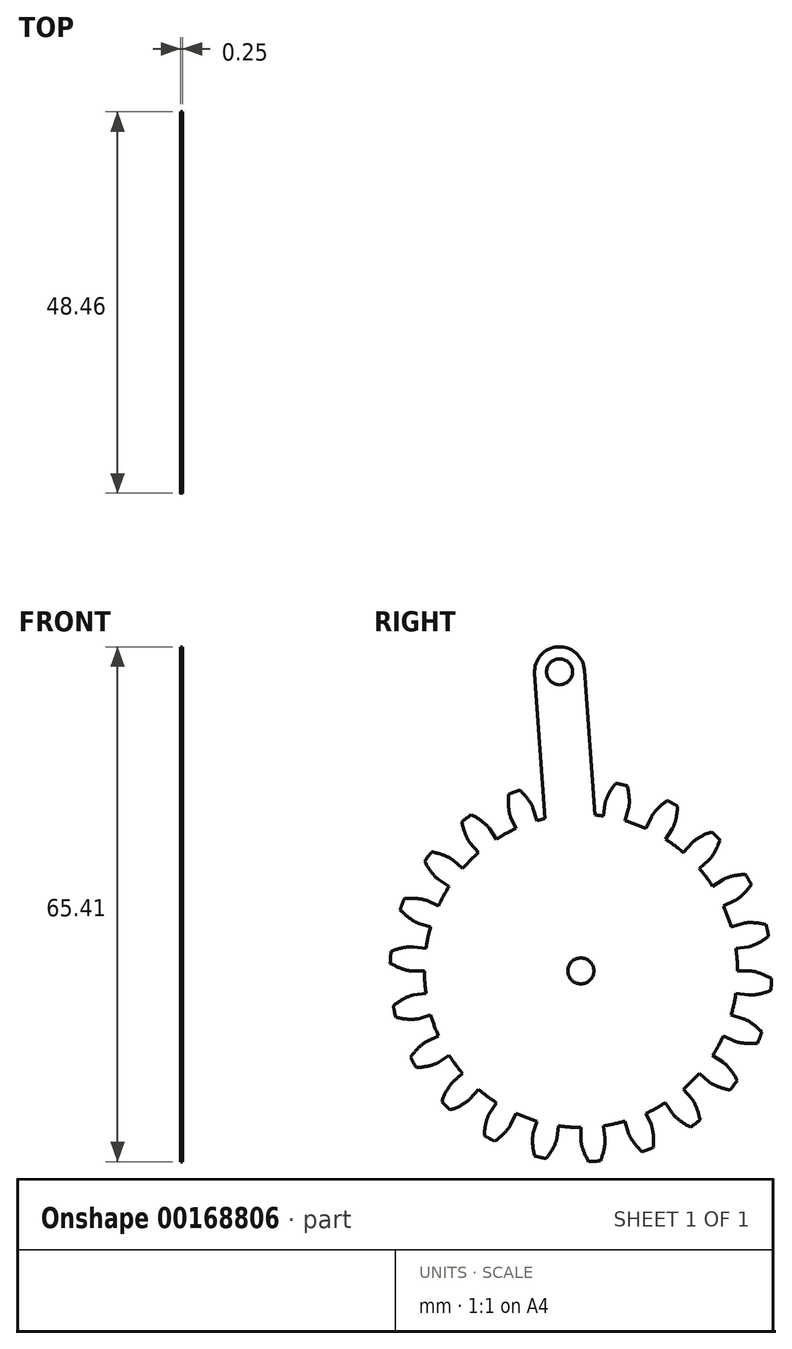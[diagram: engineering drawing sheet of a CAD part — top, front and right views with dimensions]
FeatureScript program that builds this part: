
annotation { "Feature Type Name" : "Feature", "Feature Type Description" : "" }
export const myFeature = defineFeature(function(context is Context, id is Id, definition is map)
    precondition{}
    {
        {
            assignVariable(context, id + "F0", {"name" : "NumberTeeth", "anyValue" : 22});
        }
        {
            assignVariable(context, id + "F1", {"name" : "GearThickness", "anyValue" : 0.25});
        }
        {
            var Q0;
            Q0=qCreatedBy(makeId("Right.planeOp"),FACE);
            var sketch = newSketch(context, id + "F2", { "sketchPlane" : qUnion([Q0])});
            skCircle(sketch, "E0", {"center": v(0, 0) * mm, "radius": 19.89 * mm});
            skCircle(sketch, "E1", {"center": v(0, 0) * mm, "radius": 21.52 * mm, "construction": true});
            skCircle(sketch, "E2", {"center": v(0, 0) * mm, "radius": 22.22 * mm, "construction": true});
            skCircle(sketch, "E3", {"center": v(0, 0) * mm, "radius": 24.25 * mm});
            skLineSegment(sketch, "E4", {"start": v(0, 0) * mm, "end": v(-21.52, 0) * mm, "construction": true});
            skLineSegment(sketch, "E5.1.0", {"start": v(0, 0) * mm, "end": v(-21.5, 1.08) * mm, "construction": true});
            skLineSegment(sketch, "E5.2.0", {"start": v(0, 0) * mm, "end": v(-21.4, 2.15) * mm, "construction": true});
            skLineSegment(sketch, "E5.3.0", {"start": v(0, 0) * mm, "end": v(-21.28, 3.22) * mm, "construction": true});
            skLineSegment(sketch, "E5.4.0", {"start": v(0, 0) * mm, "end": v(-21.09, 4.27) * mm, "construction": true});
            skLineSegment(sketch, "E5.5.0", {"start": v(0, 0) * mm, "end": v(-20.85, 5.32) * mm, "construction": true});
            skLineSegment(sketch, "E5.6.0", {"start": v(0, 0) * mm, "end": v(-20.56, 6.36) * mm, "construction": true});
            skLineSegment(sketch, "E5.7.0", {"start": v(0, 0) * mm, "end": v(-20.21, 7.38) * mm, "construction": true});
            skLineSegment(sketch, "E5.8.0", {"start": v(0, 0) * mm, "end": v(-19.82, 8.38) * mm, "construction": true});
            skLineSegment(sketch, "E5.9.0", {"start": v(0, 0) * mm, "end": v(-19.37, 9.36) * mm, "construction": true});
            skLineSegment(sketch, "E5.10.0", {"start": v(0, 0) * mm, "end": v(-18.88, 10.32) * mm, "construction": true});
            skLineSegment(sketch, "E5.11.0", {"start": v(0, 0) * mm, "end": v(-18.34, 11.25) * mm, "construction": true});
            skLineSegment(sketch, "E5.12.0", {"start": v(0, 0) * mm, "end": v(-17.76, 12.15) * mm, "construction": true});
            skLineSegment(sketch, "E5.13.0", {"start": v(0, 0) * mm, "end": v(-17.13, 13.02) * mm, "construction": true});
            skLineSegment(sketch, "E5.14.0", {"start": v(0, 0) * mm, "end": v(-16.46, 13.86) * mm, "construction": true});
            skLineSegment(sketch, "E5.anchor2", {"start": v(0, 0) * mm, "end": v(-16.46, 13.86) * mm, "construction": true});
            skLineSegment(sketch, "E6", {"start": v(-21.5, 1.08) * mm, "end": v(-21.54, 0) * mm, "construction": true});
            skLineSegment(sketch, "E7", {"start": v(-21.4, 2.15) * mm, "end": v(-21.62, 0) * mm, "construction": true});
            skLineSegment(sketch, "E8", {"start": v(-21.28, 3.22) * mm, "end": v(-21.76, 0.02) * mm, "construction": true});
            skLineSegment(sketch, "E9", {"start": v(-20.85, 5.32) * mm, "end": v(-22.18, 0.11) * mm, "construction": true});
            skLineSegment(sketch, "E10", {"start": v(-20.56, 6.36) * mm, "end": v(-22.46, 0.2) * mm, "construction": true});
            skLineSegment(sketch, "E11", {"start": v(-20.21, 7.38) * mm, "end": v(-22.8, 0.3) * mm, "construction": true});
            skLineSegment(sketch, "E12", {"start": v(-19.82, 8.38) * mm, "end": v(-23.17, 0.45) * mm, "construction": true});
            skLineSegment(sketch, "E13", {"start": v(-19.37, 9.36) * mm, "end": v(-23.59, 0.64) * mm, "construction": true});
            skLineSegment(sketch, "E14", {"start": v(-18.88, 10.32) * mm, "end": v(-24.04, 0.87) * mm, "construction": true});
            skLineSegment(sketch, "E15", {"start": v(-18.34, 11.25) * mm, "end": v(-24.53, 1.16) * mm, "construction": true});
            skLineSegment(sketch, "E16", {"start": v(-21.09, 4.27) * mm, "end": v(-21.94, 0.06) * mm, "construction": true});
            skLineSegment(sketch, "E17", {"start": v(-17.76, 12.15) * mm, "end": v(-25.05, 1.5) * mm, "construction": true});
            skLineSegment(sketch, "E18", {"start": v(-17.13, 13.02) * mm, "end": v(-25.6, 1.89) * mm, "construction": true});
            skLineSegment(sketch, "E19", {"start": v(-16.46, 13.86) * mm, "end": v(-26.16, 2.34) * mm, "construction": true});
            skLineSegment(sketch, "E20", {"start": v(0, 0) * mm, "end": v(-21.46, 1.54) * mm, "construction": true});
            skLineSegment(sketch, "E21", {"start": v(-19.89, 0) * mm, "end": v(-21.52, 0) * mm});
            skLineSegment(sketch, "E22.MirrorCS", {"start": v(-19.68, 2.83) * mm, "end": v(-21.3, 3.06) * mm});
            skFitSpline(sketch, "E23", {"points": [v(-21.52, 0) * mm, v(-21.54, 0) * mm, v(-21.62, 0) * mm, v(-21.76, 0.02) * mm, v(-21.94, 0.06) * mm, v(-22.18, 0.11) * mm, v(-22.46, 0.2) * mm, v(-22.8, 0.3) * mm, v(-23.17, 0.45) * mm, v(-23.59, 0.64) * mm, v(-24.04, 0.87) * mm, v(-24.53, 1.16) * mm, v(-25.05, 1.5) * mm, v(-25.6, 1.89) * mm, v(-26.16, 2.34) * mm], "startDerivative": vector(-0.77, 0) * mm, "endDerivative": vector(-1.36, 1.15) * mm});
            skLineSegment(sketch, "E24", {"start": v(-21.81, -1.32) * mm, "end": v(-26.16, 2.34) * mm, "construction": true});
            skFitSpline(sketch, "E25.MirrorCS", {"points": [v(-21.3, 3.06) * mm, v(-21.32, 3.07) * mm, v(-21.4, 3.07) * mm, v(-21.54, 3.07) * mm, v(-21.73, 3.07) * mm, v(-21.97, 3.05) * mm, v(-22.26, 3) * mm, v(-22.6, 2.94) * mm, v(-23, 2.85) * mm, v(-23.44, 2.72) * mm, v(-23.92, 2.56) * mm, v(-24.44, 2.35) * mm, v(-25, 2.09) * mm, v(-25.6, 1.77) * mm, v(-26.23, 1.4) * mm], "startDerivative": vector(-0.77, 0.11) * mm, "endDerivative": vector(-1.51, -0.94) * mm});
            skSolve(sketch);
        }
        {
            var Q0;
            {var subQ0=sQuery(id+"F2.wireOp",EDGE,"E0");var subQ27=makeQuery(id+"F2.imprint","INTERSECT",VERTEX,{"derivedFrom":[subQ0,sQuery(id+"F2.wireOp",EDGE,"10ea1024-8cf5-41f5-a75f-a634b86921f3.10.0")]});Q0=makeQuery(id+"F2.imprint","IMPRINT",FACE,{"disambiguationData":[TD([[makeQuery(id+"F2.imprint","IMPRINT",EDGE,{"disambiguationData":[TD([[subQ27,-1.0]])],"derivedFrom":subQ0}),1.0]])]});}
            var Q1;
            {var subQ0=sQuery(id+"F2.wireOp",EDGE,"10ea1024-8cf5-41f5-a75f-a634b86921f3.1.0");Q1=makeQuery(id+"F2.imprint","IMPRINT",FACE,{"disambiguationData":[TD([[makeQuery(id+"F2.imprint","IMPRINT",EDGE,{"derivedFrom":subQ0}),-1.0]])]});}
            var Q2;
            {var subQ7=sQuery(id+"F2.wireOp",EDGE,"10ea1024-8cf5-41f5-a75f-a634b86921f3.2.0");Q2=makeQuery(id+"F2.imprint","IMPRINT",FACE,{"disambiguationData":[TD([[makeQuery(id+"F2.imprint","IMPRINT",EDGE,{"derivedFrom":subQ7}),-1.0]])]});}
            var Q3;
            {var subQ8=sQuery(id+"F2.wireOp",EDGE,"10ea1024-8cf5-41f5-a75f-a634b86921f3.3.0");Q3=makeQuery(id+"F2.imprint","IMPRINT",FACE,{"disambiguationData":[TD([[makeQuery(id+"F2.imprint","IMPRINT",EDGE,{"derivedFrom":subQ8}),-1.0]])]});}
            var Q4;
            {var subQ2=sQuery(id+"F2.wireOp",EDGE,"10ea1024-8cf5-41f5-a75f-a634b86921f3.4.0");Q4=makeQuery(id+"F2.imprint","IMPRINT",FACE,{"disambiguationData":[TD([[makeQuery(id+"F2.imprint","IMPRINT",EDGE,{"derivedFrom":subQ2}),-1.0]])]});}
            var Q5;
            {var subQ8=sQuery(id+"F2.wireOp",EDGE,"10ea1024-8cf5-41f5-a75f-a634b86921f3.5.0");Q5=makeQuery(id+"F2.imprint","IMPRINT",FACE,{"disambiguationData":[TD([[makeQuery(id+"F2.imprint","IMPRINT",EDGE,{"derivedFrom":subQ8}),-1.0]])]});}
            var Q6;
            {var subQ3=sQuery(id+"F2.wireOp",EDGE,"10ea1024-8cf5-41f5-a75f-a634b86921f3.6.0");Q6=makeQuery(id+"F2.imprint","IMPRINT",FACE,{"disambiguationData":[TD([[makeQuery(id+"F2.imprint","IMPRINT",EDGE,{"derivedFrom":subQ3}),-1.0]])]});}
            var Q7;
            {var subQ0=sQuery(id+"F2.wireOp",EDGE,"10ea1024-8cf5-41f5-a75f-a634b86921f3.7.0");Q7=makeQuery(id+"F2.imprint","IMPRINT",FACE,{"disambiguationData":[TD([[makeQuery(id+"F2.imprint","IMPRINT",EDGE,{"derivedFrom":subQ0}),-1.0]])]});}
            var Q8;
            {var subQ5=sQuery(id+"F2.wireOp",EDGE,"10ea1024-8cf5-41f5-a75f-a634b86921f3.8.0");Q8=makeQuery(id+"F2.imprint","IMPRINT",FACE,{"disambiguationData":[TD([[makeQuery(id+"F2.imprint","IMPRINT",EDGE,{"derivedFrom":subQ5}),-1.0]])]});}
            var Q9;
            {var subQ1=sQuery(id+"F2.wireOp",EDGE,"10ea1024-8cf5-41f5-a75f-a634b86921f3.9.0");Q9=makeQuery(id+"F2.imprint","IMPRINT",FACE,{"disambiguationData":[TD([[makeQuery(id+"F2.imprint","IMPRINT",EDGE,{"derivedFrom":subQ1}),-1.0]])]});}
            var Q10;
            {var subQ5=sQuery(id+"F2.wireOp",EDGE,"10ea1024-8cf5-41f5-a75f-a634b86921f3.10.0");Q10=makeQuery(id+"F2.imprint","IMPRINT",FACE,{"disambiguationData":[TD([[makeQuery(id+"F2.imprint","IMPRINT",EDGE,{"derivedFrom":subQ5}),-1.0]])]});}
            var Q11;
            {var subQ8=sQuery(id+"F2.wireOp",EDGE,"10ea1024-8cf5-41f5-a75f-a634b86921f3.11.0");Q11=makeQuery(id+"F2.imprint","IMPRINT",FACE,{"disambiguationData":[TD([[makeQuery(id+"F2.imprint","IMPRINT",EDGE,{"derivedFrom":subQ8}),-1.0]])]});}
            var Q12;
            {var subQ2=sQuery(id+"F2.wireOp",EDGE,"10ea1024-8cf5-41f5-a75f-a634b86921f3.12.0");Q12=makeQuery(id+"F2.imprint","IMPRINT",FACE,{"disambiguationData":[TD([[makeQuery(id+"F2.imprint","IMPRINT",EDGE,{"derivedFrom":subQ2}),-1.0]])]});}
            var Q13;
            {var subQ3=sQuery(id+"F2.wireOp",EDGE,"10ea1024-8cf5-41f5-a75f-a634b86921f3.13.0");Q13=makeQuery(id+"F2.imprint","IMPRINT",FACE,{"disambiguationData":[TD([[makeQuery(id+"F2.imprint","IMPRINT",EDGE,{"derivedFrom":subQ3}),-1.0]])]});}
            var Q14;
            {var subQ0=sQuery(id+"F2.wireOp",EDGE,"10ea1024-8cf5-41f5-a75f-a634b86921f3.14.0");Q14=makeQuery(id+"F2.imprint","IMPRINT",FACE,{"disambiguationData":[TD([[makeQuery(id+"F2.imprint","IMPRINT",EDGE,{"derivedFrom":subQ0}),-1.0]])]});}
            var Q15;
            {var subQ6=sQuery(id+"F2.wireOp",EDGE,"10ea1024-8cf5-41f5-a75f-a634b86921f3.15.0");Q15=makeQuery(id+"F2.imprint","IMPRINT",FACE,{"disambiguationData":[TD([[makeQuery(id+"F2.imprint","IMPRINT",EDGE,{"derivedFrom":subQ6}),-1.0]])]});}
            var Q16;
            {var subQ5=sQuery(id+"F2.wireOp",EDGE,"10ea1024-8cf5-41f5-a75f-a634b86921f3.16.0");Q16=makeQuery(id+"F2.imprint","IMPRINT",FACE,{"disambiguationData":[TD([[makeQuery(id+"F2.imprint","IMPRINT",EDGE,{"derivedFrom":subQ5}),-1.0]])]});}
            var Q17;
            {var subQ7=sQuery(id+"F2.wireOp",EDGE,"10ea1024-8cf5-41f5-a75f-a634b86921f3.17.0");Q17=makeQuery(id+"F2.imprint","IMPRINT",FACE,{"disambiguationData":[TD([[makeQuery(id+"F2.imprint","IMPRINT",EDGE,{"derivedFrom":subQ7}),-1.0]])]});}
            var Q18;
            {var subQ5=sQuery(id+"F2.wireOp",EDGE,"10ea1024-8cf5-41f5-a75f-a634b86921f3.18.0");Q18=makeQuery(id+"F2.imprint","IMPRINT",FACE,{"disambiguationData":[TD([[makeQuery(id+"F2.imprint","IMPRINT",EDGE,{"derivedFrom":subQ5}),-1.0]])]});}
            var Q19;
            {var subQ8=sQuery(id+"F2.wireOp",EDGE,"10ea1024-8cf5-41f5-a75f-a634b86921f3.19.0");Q19=makeQuery(id+"F2.imprint","IMPRINT",FACE,{"disambiguationData":[TD([[makeQuery(id+"F2.imprint","IMPRINT",EDGE,{"derivedFrom":subQ8}),-1.0]])]});}
            var Q20;
            {var subQ8=sQuery(id+"F2.wireOp",EDGE,"E21");Q20=makeQuery(id+"F2.imprint","IMPRINT",FACE,{"disambiguationData":[TD([[makeQuery(id+"F2.imprint","IMPRINT",EDGE,{"derivedFrom":subQ8}),-1.0]])]});}
            extrude(context, id + "F3", {"entities" : qUnion([Q0, Q1, Q2, Q3, Q4, Q5, Q6, Q7, Q8, Q9, Q10, Q11, Q12, Q13, Q14, Q15, Q16, Q17, Q18, Q19, Q20]), "depth" : (getVariable(context, 'GearThickness')) * mm});
        }
        {
            var Q0;
            Q0=makeQuery(id+"F3.opExtrude","SWEPT_FACE",FACE,{"disambiguationData":[OSD([sQuery(id+"F2.wireOp",EDGE,"E25.MirrorCS")])]});
            var Q1;
            Q1=makeQuery(id+"F3.opExtrude","SWEPT_FACE",FACE,{"disambiguationData":[OSD([sQuery(id+"F2.wireOp",EDGE,"E23")])]});
            var Q2;
            Q2=makeQuery(id+"F3.opExtrude","SWEPT_FACE",FACE,{"disambiguationData":[OSD([sQuery(id+"F2.wireOp",EDGE,"E3")])]});
            var Q3;
            Q3=makeQuery(id+"F3.opExtrude","SWEPT_FACE",FACE,{"disambiguationData":[OSD([sQuery(id+"F2.wireOp",EDGE,"E22.MirrorCS")])]});
            var Q4;
            Q4=makeQuery(id+"F3.opExtrude","SWEPT_FACE",FACE,{"disambiguationData":[OSD([sQuery(id+"F2.wireOp",EDGE,"E21")])]});
            var Q5;
            Q5=makeQuery(id+"F3.opExtrude","SWEPT_FACE",FACE,{"disambiguationData":[OSD([sQuery(id+"F2.wireOp",EDGE,"E0")])]});
            circularPattern(context, id + "F4", {"faces" : qUnion([Q0, Q1, Q2, Q3, Q4]), "axis" : qUnion([Q5]), "angle" : 360 * degree, "instanceCount" : getVariable(context, 'NumberTeeth'), "equalSpace" : true, "patternType" : PatternType.FACE});
        }
        {
            var Q0;
            Q0=makeQuery(id+"F3.opExtrude","CAP_FACE",FACE,{"disambiguationData":[OSD([sQuery(id+"F2.wireOp",EDGE,"E0"),sQuery(id+"F2.wireOp",EDGE,"E3"),sQuery(id+"F2.wireOp",EDGE,"E21"),sQuery(id+"F2.wireOp",EDGE,"E22.MirrorCS"),sQuery(id+"F2.wireOp",EDGE,"E23"),sQuery(id+"F2.wireOp",EDGE,"E25.MirrorCS")])],"isStart":false});
            var sketch = newSketch(context, id + "F5", { "sketchPlane" : qUnion([Q0])});
            skCircle(sketch, "E26", {"center": v(0, 0) * mm, "radius": 1.65 * mm});
            skSolve(sketch);
        }
        {
            var Q0;
            Q0 = qSketchRegion(id + "F5", true);
            var Q1;
            Q1=makeQuery(id+"F3.opExtrude","CAP_FACE",FACE,{"disambiguationData":[OSD([sQuery(id+"F2.wireOp",EDGE,"E0"),sQuery(id+"F2.wireOp",EDGE,"E3"),sQuery(id+"F2.wireOp",EDGE,"E21"),sQuery(id+"F2.wireOp",EDGE,"E22.MirrorCS"),sQuery(id+"F2.wireOp",EDGE,"E23"),sQuery(id+"F2.wireOp",EDGE,"E25.MirrorCS")])],"isStart":true});
            extrude(context, id + "F6", {"entities" : qUnion([Q0]), "operationType" : NewBodyOperationType.REMOVE, "endBound" : BoundingType.UP_TO_SURFACE, "oppositeDirection" : true, "endBoundEntityFace" : qUnion([Q1]), "depth" : 25.4 * mm});
        }
        {
            var Q0;
            Q0=makeQuery(id+"F3.opExtrude","CAP_FACE",FACE,{"disambiguationData":[OSD([sQuery(id+"F2.wireOp",EDGE,"E0"),sQuery(id+"F2.wireOp",EDGE,"E3"),sQuery(id+"F2.wireOp",EDGE,"E21"),sQuery(id+"F2.wireOp",EDGE,"E22.MirrorCS"),sQuery(id+"F2.wireOp",EDGE,"E23"),sQuery(id+"F2.wireOp",EDGE,"E25.MirrorCS")])],"isStart":false});
            var sketch = newSketch(context, id + "F7", { "sketchPlane" : qUnion([Q0])});
            skLineSegment(sketch, "E27", {"start": v(0, 0) * mm, "end": v(-1.73, 24.18) * mm});
            skLineSegment(sketch, "E28", {"start": v(-1.73, 24.18) * mm, "end": v(-2.72, 38) * mm});
            skCircle(sketch, "E29", {"center": v(-2.72, 38) * mm, "radius": 1.65 * mm});
            skLineSegment(sketch, "E30", {"start": v(-6.11, 40.94) * mm, "end": v(-2.94, -3.4) * mm});
            skLineSegment(sketch, "E31", {"start": v(0.22, 41.4) * mm, "end": v(3.4, -2.94) * mm});
            skLineSegment(sketch, "E32", {"start": v(-6.11, 40.94) * mm, "end": v(0.22, 41.4) * mm});
            skLineSegment(sketch, "E33", {"start": v(-2.94, -3.4) * mm, "end": v(3.4, -2.94) * mm});
            skSolve(sketch);
        }
        {
            var Q0;
            Q0 = qSketchRegion(id + "F7", true);
            var Q1;
            Q1=makeQuery(id+"F3.opExtrude","CAP_FACE",FACE,{"disambiguationData":[OSD([sQuery(id+"F2.wireOp",EDGE,"E0"),sQuery(id+"F2.wireOp",EDGE,"E3"),sQuery(id+"F2.wireOp",EDGE,"E21"),sQuery(id+"F2.wireOp",EDGE,"E22.MirrorCS"),sQuery(id+"F2.wireOp",EDGE,"E23"),sQuery(id+"F2.wireOp",EDGE,"E25.MirrorCS")])],"isStart":true});
            extrude(context, id + "F8", {"entities" : qUnion([Q0]), "operationType" : NewBodyOperationType.ADD, "endBound" : BoundingType.UP_TO_SURFACE, "oppositeDirection" : true, "endBoundEntityFace" : qUnion([Q1]), "depth" : 25.4 * mm});
        }
        {
            var Q0;
            Q0=makeQuery(id+"F8.boolean.opBoolean","MERGE",FACE,{"derivedFrom":[makeQuery(id+"F3.opExtrude","CAP_FACE",FACE,{"disambiguationData":[OSD([sQuery(id+"F2.wireOp",EDGE,"E0"),sQuery(id+"F2.wireOp",EDGE,"E3"),sQuery(id+"F2.wireOp",EDGE,"E21"),sQuery(id+"F2.wireOp",EDGE,"E22.MirrorCS"),sQuery(id+"F2.wireOp",EDGE,"E23"),sQuery(id+"F2.wireOp",EDGE,"E25.MirrorCS")])],"isStart":false}),makeQuery(id+"F8.opExtrude","CAP_FACE",FACE,{"disambiguationData":[OSD([sQuery(id+"F7.wireOp",EDGE,"E29"),sQuery(id+"F7.wireOp",EDGE,"E30"),sQuery(id+"F7.wireOp",EDGE,"E31"),sQuery(id+"F7.wireOp",EDGE,"E32"),sQuery(id+"F7.wireOp",EDGE,"E33")])],"isStart":true})]});
            var sketch = newSketch(context, id + "F9", { "sketchPlane" : qUnion([Q0])});
            skCircle(sketch, "E34", {"center": v(0, 0) * mm, "radius": 1.65 * mm});
            skSolve(sketch);
        }
        {
            var Q0;
            Q0 = qSketchRegion(id + "F9", true);
            var Q1;
            {var subQ0=sQuery(id+"F2.wireOp",EDGE,"E25.MirrorCS");var subQ1=sQuery(id+"F2.wireOp",EDGE,"E23");var subQ2=sQuery(id+"F2.wireOp",EDGE,"E22.MirrorCS");var subQ3=sQuery(id+"F2.wireOp",EDGE,"E21");var subQ4=sQuery(id+"F2.wireOp",EDGE,"E3");var subQ5=sQuery(id+"F2.wireOp",EDGE,"E0");Q1=makeQuery(id+"F8.boolean.opBoolean","MERGE",FACE,{"derivedFrom":[makeQuery(id+"F3.opExtrude","CAP_FACE",FACE,{"disambiguationData":[OSD([subQ5,subQ4,subQ3,subQ2,subQ1,subQ0])],"isStart":true}),makeQuery(id+"F8.opExtrude","CAP_FACE",FACE,{"disambiguationData":[OSD([subQ5,subQ4,subQ3,subQ2,subQ1,subQ0])],"isStart":false})]});}
            extrude(context, id + "F10", {"entities" : qUnion([Q0]), "operationType" : NewBodyOperationType.REMOVE, "endBound" : BoundingType.UP_TO_SURFACE, "oppositeDirection" : true, "endBoundEntityFace" : qUnion([Q1]), "depth" : 25.4 * mm});
        }
        {
            var Q0;
            Q0=makeQuery(id+"F8.opExtrude","SWEPT_EDGE",EDGE,{"disambiguationData":[OSD([sQuery(id+"F7.wireOp",EDGE,"E31"),sQuery(id+"F7.wireOp",EDGE,"E32")])]});
            var Q1;
            Q1=makeQuery(id+"F8.opExtrude","SWEPT_EDGE",EDGE,{"disambiguationData":[OSD([sQuery(id+"F7.wireOp",EDGE,"E30"),sQuery(id+"F7.wireOp",EDGE,"E32")])]});
            fillet(context, id + "F11", {"entities" : qUnion([Q0, Q1]), "radius" : 3.17 * mm, "tangentPropagation" : true, "allowEdgeOverflow" : false});
        }
    });
